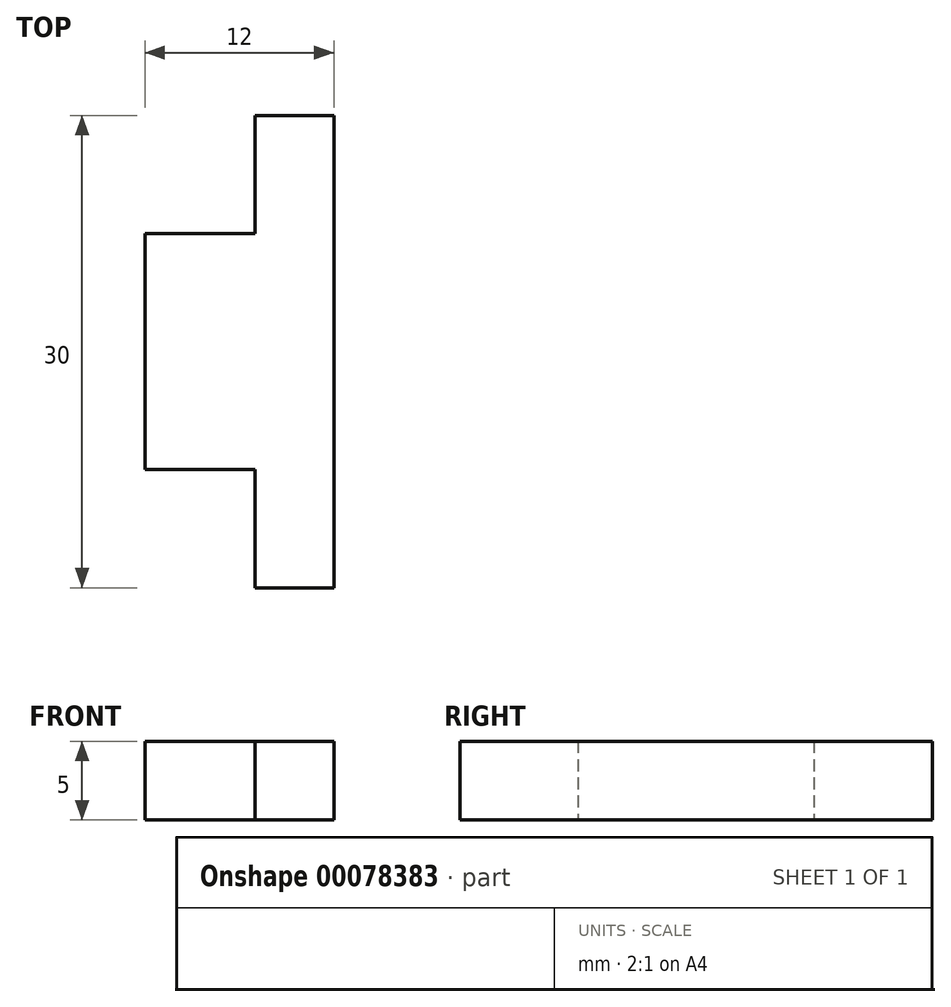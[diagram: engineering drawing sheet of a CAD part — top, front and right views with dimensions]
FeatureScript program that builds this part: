
annotation { "Feature Type Name" : "Feature", "Feature Type Description" : "" }
export const myFeature = defineFeature(function(context is Context, id is Id, definition is map)
    precondition{}
    {
        {
            var Q0;
            Q0=qCreatedBy(makeId("Top.planeOp"),FACE);
            var sketch = newSketch(context, id + "F0", { "sketchPlane" : qUnion([Q0])});
            skLineSegment(sketch, "E0.bottom", {"start": v(2.5, 15) * mm, "end": v(-2.5, 15) * mm});
            skLineSegment(sketch, "E0.top", {"start": v(2.5, -15) * mm, "end": v(-2.5, -15) * mm});
            skLineSegment(sketch, "E0.left", {"start": v(2.5, 15) * mm, "end": v(2.5, -15) * mm});
            skLineSegment(sketch, "E0.right", {"start": v(-2.5, 15) * mm, "end": v(-2.5, -15) * mm});
            skPoint(sketch, "E0.middle", {"position": v(0, 0) * mm});
            skLineSegment(sketch, "E1", {"start": v(-2.5, -7.5) * mm, "end": v(-9.5, -7.5) * mm});
            skLineSegment(sketch, "E2", {"start": v(-9.5, -7.5) * mm, "end": v(-9.5, 7.5) * mm});
            skLineSegment(sketch, "E3", {"start": v(-9.5, 7.5) * mm, "end": v(-2.5, 7.5) * mm});
            skLineSegment(sketch, "E4", {"start": v(-9.5, 0) * mm, "end": v(0, 0) * mm, "construction": true});
            skSolve(sketch);
        }
        {
            var Q0;
            Q0 = qSketchRegion(id + "F0", true);
            extrude(context, id + "F1", {"entities" : qUnion([Q0]), "depth" : 5 * mm});
        }
    });
